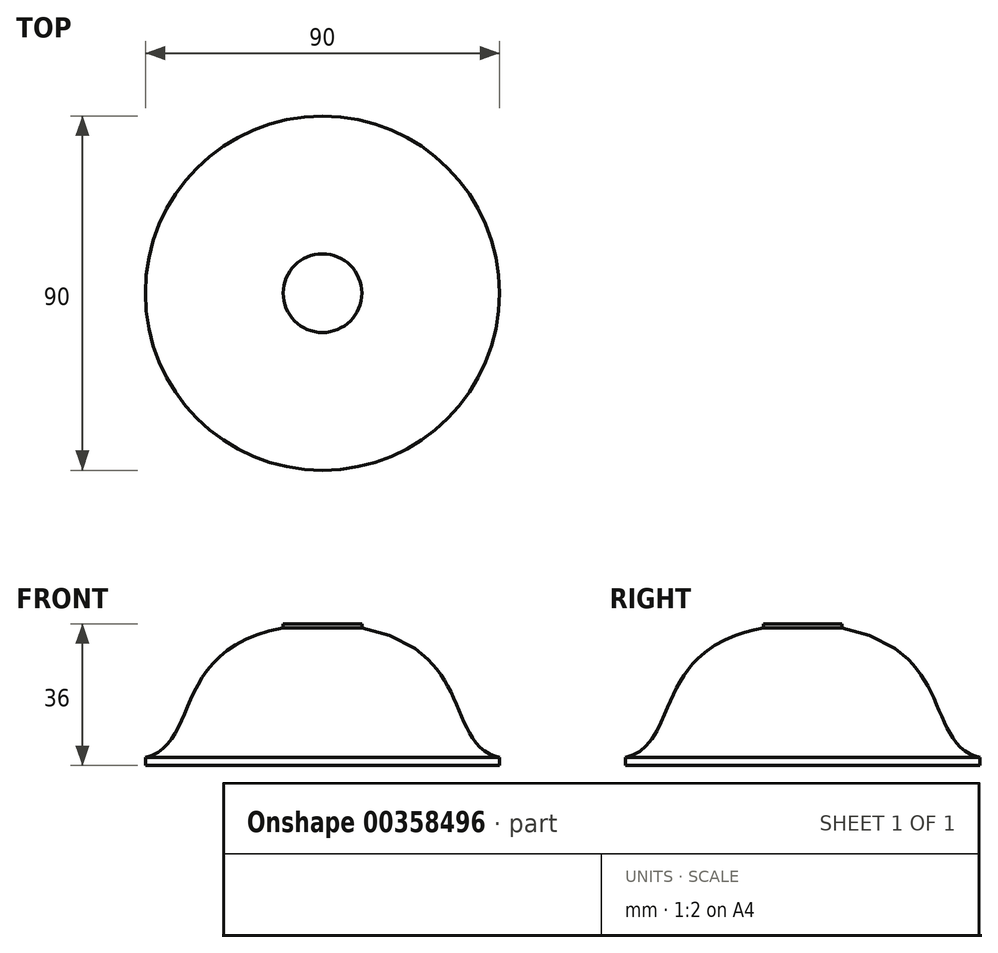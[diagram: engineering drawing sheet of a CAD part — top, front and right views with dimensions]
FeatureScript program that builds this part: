
annotation { "Feature Type Name" : "Feature", "Feature Type Description" : "" }
export const myFeature = defineFeature(function(context is Context, id is Id, definition is map)
    precondition{}
    {
        {
            var Q0;
            Q0=qCreatedBy(makeId("Front.planeOp"),FACE);
            var sketch = newSketch(context, id + "F0", { "sketchPlane" : qUnion([Q0])});
            skLineSegment(sketch, "E0", {"start": v(0, 0) * mm, "end": v(0, 35) * mm});
            skLineSegment(sketch, "E1", {"start": v(0, 0) * mm, "end": v(45, 0) * mm});
            skLineSegment(sketch, "E2", {"start": v(0, 35) * mm, "end": v(10, 35) * mm});
            skLineSegment(sketch, "E3", {"start": v(45, 0) * mm, "end": v(45, 2) * mm});
            skFitSpline(sketch, "E4", {"points": [v(10, 35) * mm, v(45, 2) * mm], "startDerivative": vector(87.02, -16.31) * mm, "endDerivative": vector(42.67, -10.06) * mm});
            skSolve(sketch);
        }
        {
            var Q0;
            Q0 = qSketchRegion(id + "F0", true);
            var Q1;
            Q1=sQuery(id+"F0.wireOp",EDGE,"E0");
            revolve(context, id + "F1", {"entities" : qUnion([Q0]), "axis" : qUnion([Q1]), "revolveType" : RevolveType.FULL});
        }
        {
            var Q0;
            Q0=makeQuery(id+"F1.opRevolve","SWEPT_FACE",FACE,{"disambiguationData":[OSD([sQuery(id+"F0.wireOp",EDGE,"E2")])]});
            extrude(context, id + "F2", {"entities" : qUnion([Q0]), "operationType" : NewBodyOperationType.ADD, "depth" : 1 * mm});
        }
    });
